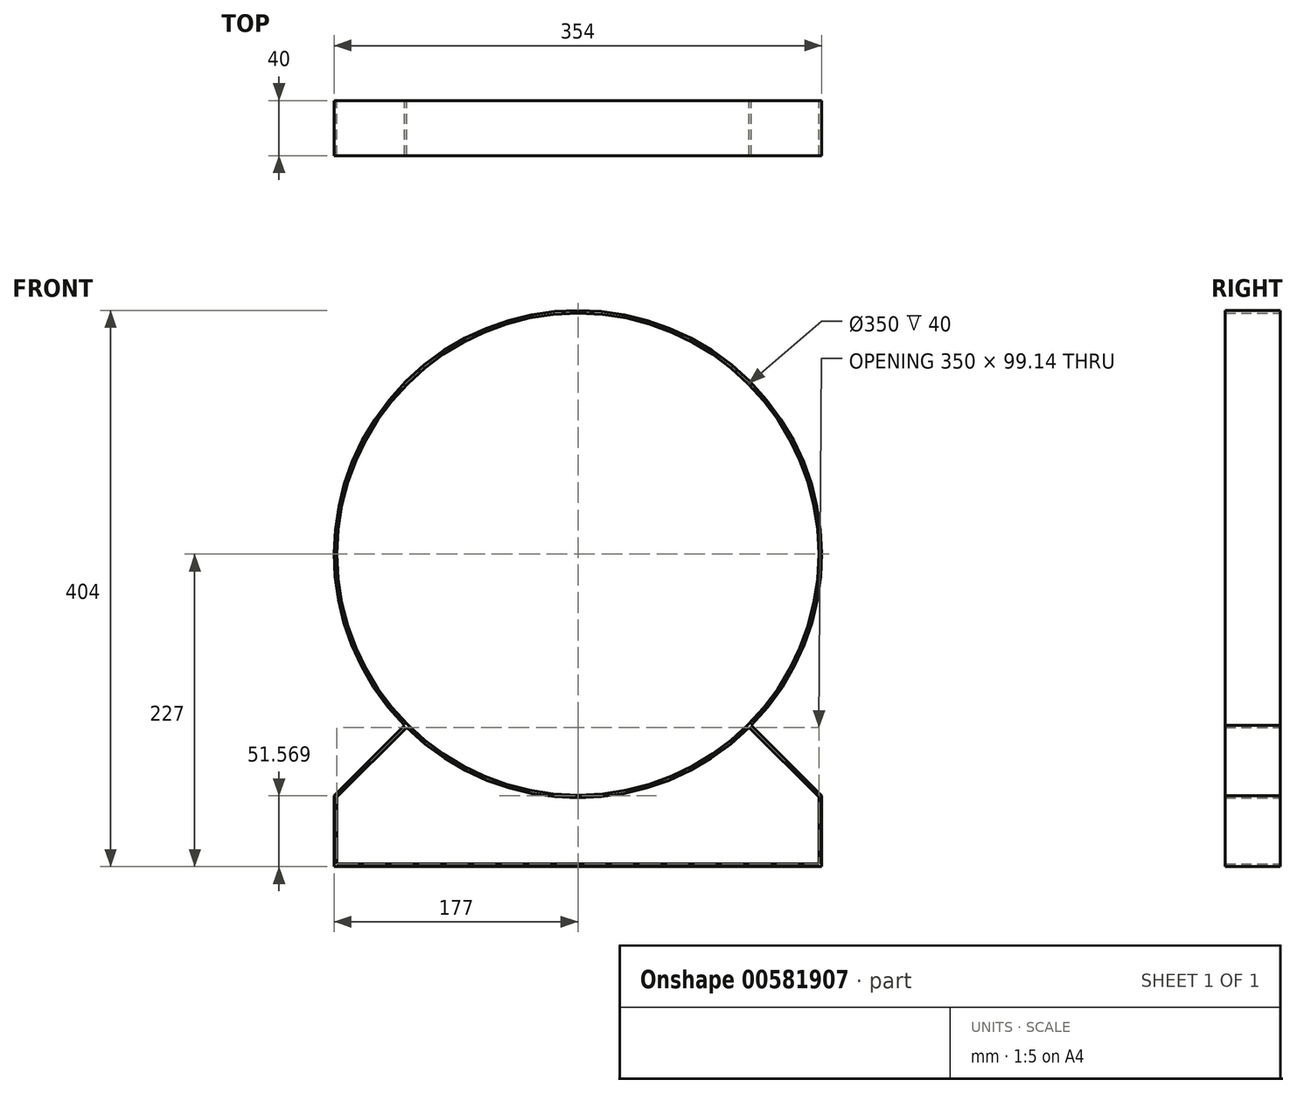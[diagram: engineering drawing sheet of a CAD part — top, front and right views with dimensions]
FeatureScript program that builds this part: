
annotation { "Feature Type Name" : "Feature", "Feature Type Description" : "" }
export const myFeature = defineFeature(function(context is Context, id is Id, definition is map)
    precondition{}
    {
        {
            var Q0;
            Q0=qCreatedBy(makeId("Front.planeOp"),FACE);
            var sketch = newSketch(context, id + "F0", { "sketchPlane" : qUnion([Q0])});
            skLineSegment(sketch, "E0", {"start": v(0, 0) * mm, "end": v(-679.96, 0) * mm, "construction": true});
            skLineSegment(sketch, "E1", {"start": v(0, 0) * mm, "end": v(0, 658.78) * mm, "construction": true});
            skLineSegment(sketch, "E2", {"start": v(0, 0) * mm, "end": v(-291.77, -291.77) * mm, "construction": true});
            skLineSegment(sketch, "E3", {"start": v(0, 0) * mm, "end": v(291.77, -291.77) * mm, "construction": true});
            skCircle(sketch, "E4", {"center": v(0, 0) * mm, "radius": 175 * mm});
            skCircle(sketch, "E5", {"center": v(0, 0) * mm, "radius": 177 * mm});
            skLineSegment(sketch, "E6", {"start": v(-177, -227) * mm, "end": v(0, -227) * mm});
            skLineSegment(sketch, "E7", {"start": v(-175, -225) * mm, "end": v(0, -225) * mm});
            skLineSegment(sketch, "E8", {"start": v(0, 0) * mm, "end": v(0, -311.11) * mm, "construction": true});
            skLineSegment(sketch, "E9", {"start": v(-175, -225) * mm, "end": v(-175, -176.41) * mm});
            skLineSegment(sketch, "E10", {"start": v(-177, -227) * mm, "end": v(-177, -175.59) * mm});
            skLineSegment(sketch, "E11", {"start": v(-125.86, -124.45) * mm, "end": v(-177, -175.59) * mm});
            skLineSegment(sketch, "E12", {"start": v(-124.45, -125.86) * mm, "end": v(-175, -176.41) * mm});
            skLineSegment(sketch, "E13.MirrorCS", {"start": v(124.45, -125.86) * mm, "end": v(175, -176.41) * mm});
            skLineSegment(sketch, "E14.MirrorCS", {"start": v(177, -227) * mm, "end": v(0, -227) * mm});
            skLineSegment(sketch, "E15.MirrorCS", {"start": v(175, -225) * mm, "end": v(0, -225) * mm});
            skLineSegment(sketch, "E16.MirrorCS", {"start": v(125.86, -124.45) * mm, "end": v(177, -175.59) * mm});
            skLineSegment(sketch, "E17.MirrorCS", {"start": v(175, -225) * mm, "end": v(175, -176.41) * mm});
            skLineSegment(sketch, "E18.MirrorCS", {"start": v(177, -227) * mm, "end": v(177, -175.59) * mm});
            skSolve(sketch);
        }
        {
            var Q0;
            Q0=qSketchRegion(id+"F0",true);
            extrude(context, id + "F1", {"entities" : qUnion([Q0]), "offsetDistance" : 25 * mm, "depth" : 40 * mm});
        }
    });
